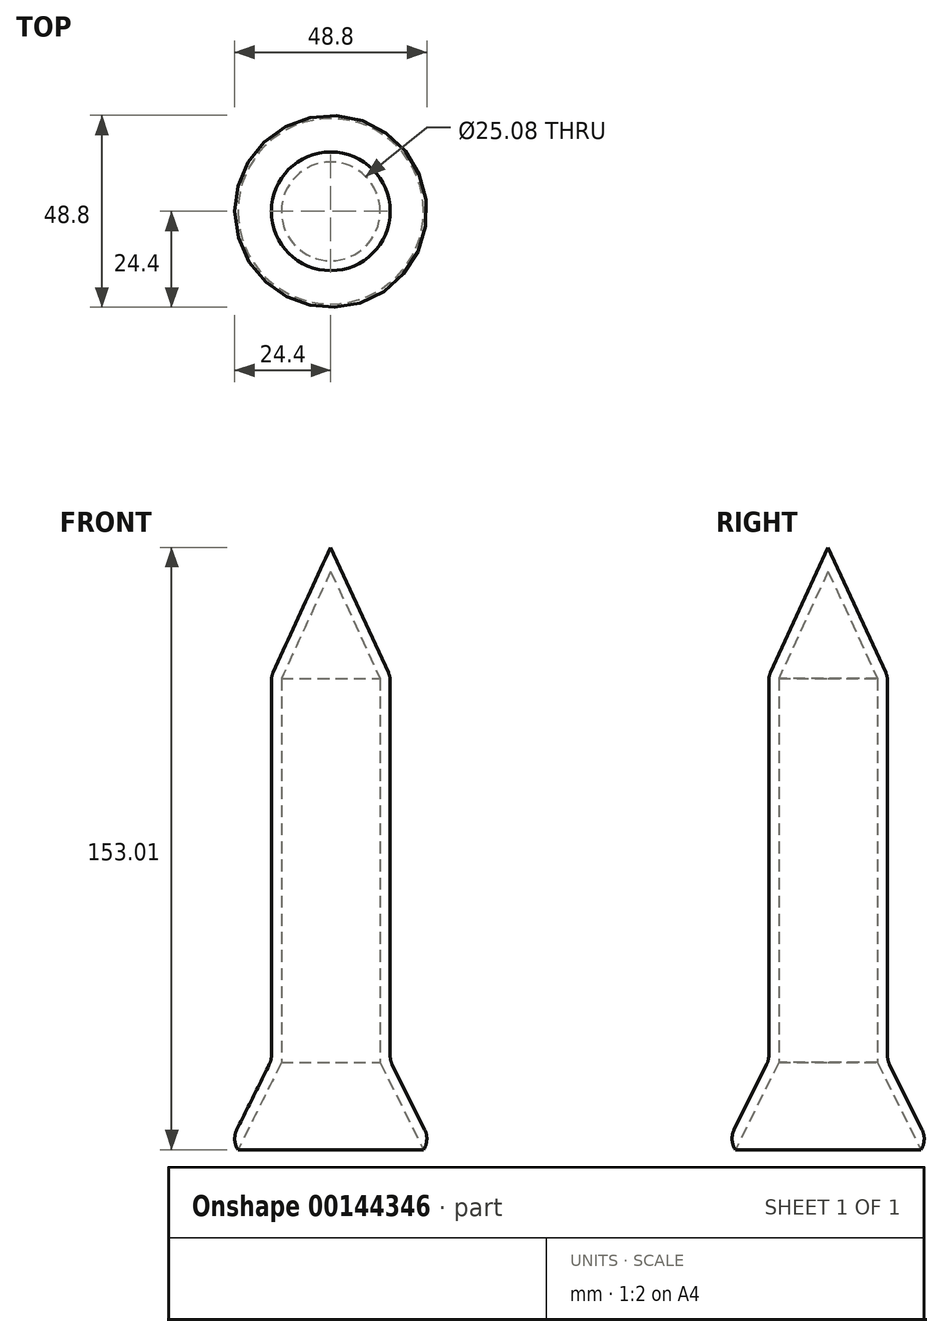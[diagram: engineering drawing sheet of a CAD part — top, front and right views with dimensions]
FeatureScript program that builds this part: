
annotation { "Feature Type Name" : "Feature", "Feature Type Description" : "" }
export const myFeature = defineFeature(function(context is Context, id is Id, definition is map)
    precondition{}
    {
        {
            var Q0;
            Q0=qCreatedBy(makeId("Right.planeOp"),FACE);
            var sketch = newSketch(context, id + "F0", { "sketchPlane" : qUnion([Q0])});
            skLineSegment(sketch, "E0", {"start": v(0, 0) * mm, "end": v(0, 75.9) * mm});
            skLineSegment(sketch, "E1", {"start": v(0, 75.9) * mm, "end": v(-15.08, 43.15) * mm});
            skLineSegment(sketch, "E2", {"start": v(-15.08, 43.15) * mm, "end": v(-15.08, -54.39) * mm});
            skLineSegment(sketch, "E3", {"start": v(-15.08, -54.39) * mm, "end": v(-26.4, -77.11) * mm});
            skLineSegment(sketch, "E4", {"start": v(-26.4, -77.11) * mm, "end": v(0, -77.11) * mm});
            skLineSegment(sketch, "E5", {"start": v(0, -77.11) * mm, "end": v(0, 0) * mm});
            skSolve(sketch);
        }
        {
            var Q0;
            Q0=makeQuery(id+"F0.imprint","IMPRINT",FACE,{"disambiguationData":[TD([[makeQuery(id+"F0.imprint","IMPRINT",EDGE,{"derivedFrom":sQuery(id+"F0.wireOp",EDGE,"E0")}),1.0]])]});
            var sketch = newSketch(context, id + "F1", { "sketchPlane" : qUnion([Q0])});
            skSolve(sketch);
        }
        {
            var Q0;
            Q0 = qSketchRegion(id + "F1", true);
            var Q1;
            Q1=makeQuery(id+"F0.imprint","IMPRINT",FACE,{"disambiguationData":[TD([[makeQuery(id+"F0.imprint","IMPRINT",EDGE,{"derivedFrom":sQuery(id+"F0.wireOp",EDGE,"E0")}),1.0]])]});
            var Q2;
            Q2=sQuery(id+"F0.wireOp",EDGE,"E0");
            revolve(context, id + "F2", {"entities" : qUnion([Q0, Q1]), "axis" : qUnion([Q2]), "revolveType" : RevolveType.FULL});
        }
        {
            var Q0;
            Q0=makeQuery(id+"F2.opRevolve","SWEPT_FACE",FACE,{"disambiguationData":[OSD([sQuery(id+"F0.wireOp",EDGE,"E4")])]});
            shell(context, id + "F3", {"entities" : qUnion([Q0]), "thickness" : 2.54 * mm});
        }
        {
            var Q0;
            Q0=makeQuery(id+"F2.opRevolve","SWEPT_FACE",FACE,{"disambiguationData":[OSD([sQuery(id+"F0.wireOp",EDGE,"E2")])]});
            fillet(context, id + "F4", {"entities" : qUnion([Q0]), "radius" : 5.08 * mm, "tangentPropagation" : true, "allowEdgeOverflow" : false});
        }
        {
            var Q0;
            Q0=makeQuery(id+"F2.opRevolve","SWEPT_FACE",FACE,{"disambiguationData":[OSD([sQuery(id+"F0.wireOp",EDGE,"E3")])]});
            fillet(context, id + "F5", {"entities" : qUnion([Q0]), "radius" : 5.08 * mm, "tangentPropagation" : true, "allowEdgeOverflow" : false});
        }
    });
